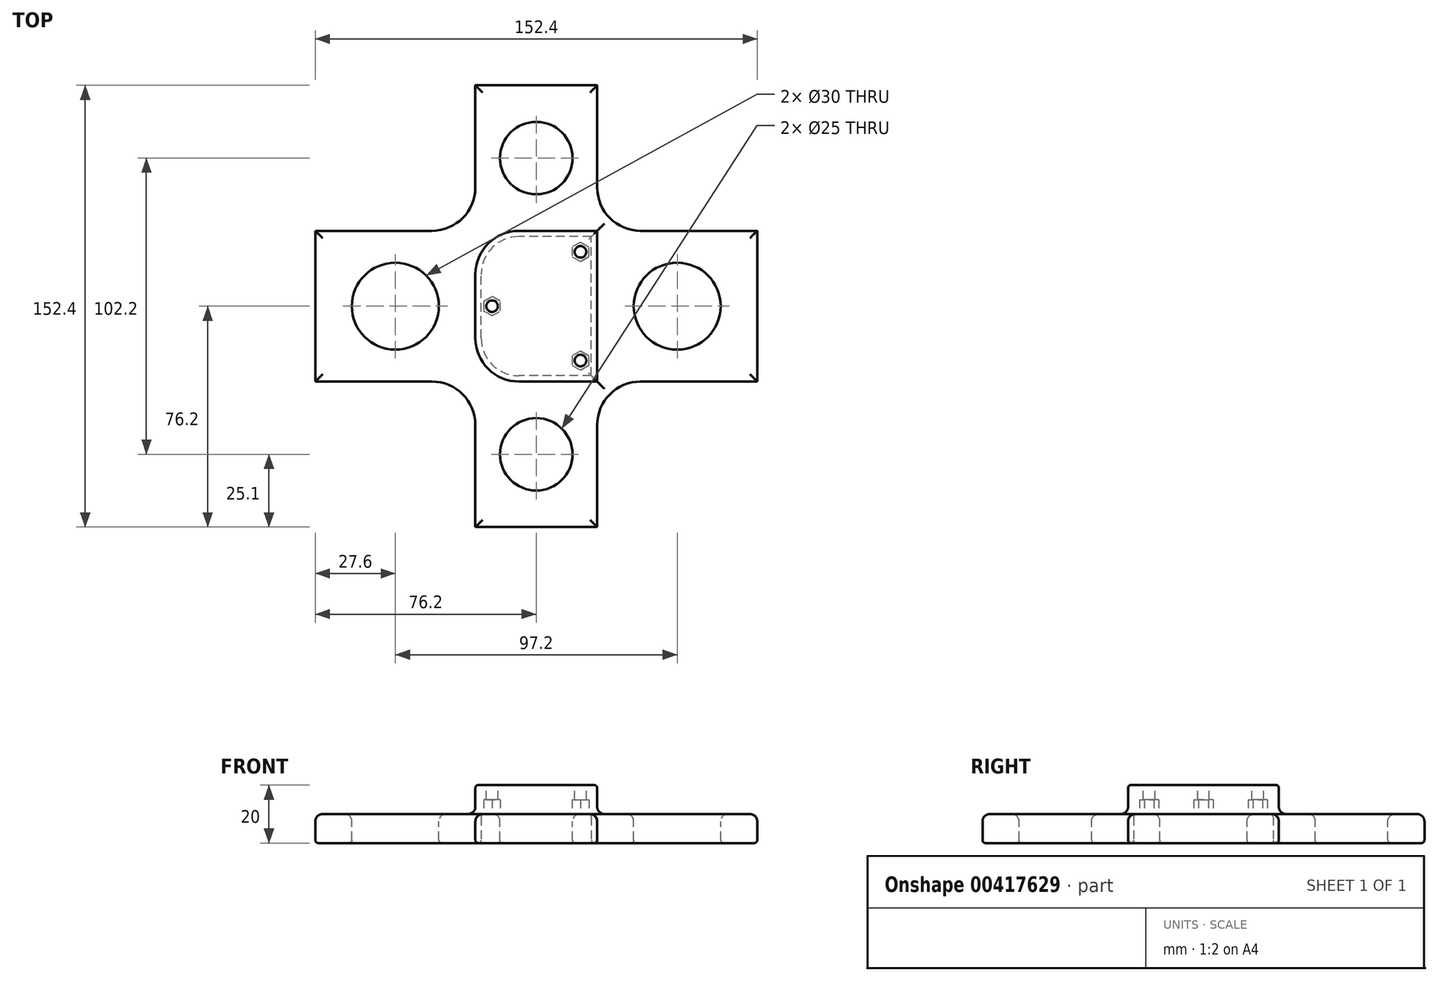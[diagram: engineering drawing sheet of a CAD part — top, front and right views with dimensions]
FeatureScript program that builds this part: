
annotation { "Feature Type Name" : "Feature", "Feature Type Description" : "" }
export const myFeature = defineFeature(function(context is Context, id is Id, definition is map)
    precondition{}
    {
        {
            var Q0;
            Q0=qCreatedBy(makeId("Top.planeOp"),FACE);
            var sketch = newSketch(context, id + "F0", { "sketchPlane" : qUnion([Q0])});
            skLineSegment(sketch, "E0.bottom", {"start": v(76.2, 76.2) * mm, "end": v(-76.2, 76.2) * mm});
            skLineSegment(sketch, "E0.top", {"start": v(76.2, -76.2) * mm, "end": v(-76.2, -76.2) * mm});
            skLineSegment(sketch, "E0.left", {"start": v(76.2, 76.2) * mm, "end": v(76.2, -76.2) * mm});
            skLineSegment(sketch, "E0.right", {"start": v(-76.2, 76.2) * mm, "end": v(-76.2, -76.2) * mm});
            skPoint(sketch, "E0.middle", {"position": v(0, 0) * mm});
            skSolve(sketch);
        }
        {
            var Q0;
            Q0 = qSketchRegion(id + "F0", true);
            extrude(context, id + "F1", {"entities" : qUnion([Q0]), "depth" : 10 * mm});
        }
        {
            var Q0;
            Q0=makeQuery(id+"F1.opExtrude","CAP_FACE",FACE,{"disambiguationData":[OSD([sQuery(id+"F0.wireOp",EDGE,"E0.bottom"),sQuery(id+"F0.wireOp",EDGE,"E0.top"),sQuery(id+"F0.wireOp",EDGE,"E0.left"),sQuery(id+"F0.wireOp",EDGE,"E0.right")])],"isStart":false});
            var sketch = newSketch(context, id + "F2", { "sketchPlane" : qUnion([Q0])});
            skLineSegment(sketch, "E1.bottom", {"start": v(21, -26) * mm, "end": v(-6, -26) * mm});
            skLineSegment(sketch, "E1.top", {"start": v(21, 26) * mm, "end": v(-6, 26) * mm});
            skLineSegment(sketch, "E1.left", {"start": v(21, -26) * mm, "end": v(21, 26) * mm});
            skLineSegment(sketch, "E1.right", {"start": v(-21, -11) * mm, "end": v(-21, 11) * mm});
            skPoint(sketch, "E1.middle", {"position": v(0, 0) * mm});
            skPoint(sketch, "E2.visualSharp", {"position": v(-21, 26) * mm});
            skArc(sketch, "E2.filletArc", {"start": v(-6, 26) * mm, "mid": v(-16.6, 21.6) * mm, "end": v(-21, 11) * mm});
            skPoint(sketch, "E3.visualSharp", {"position": v(-21, -26) * mm});
            skArc(sketch, "E3.filletArc", {"start": v(-21, -11) * mm, "mid": v(-16.6, -21.6) * mm, "end": v(-6, -26) * mm});
            skSolve(sketch);
        }
        {
            var Q0;
            Q0 = qSketchRegion(id + "F2", true);
            extrude(context, id + "F3", {"entities" : qUnion([Q0]), "operationType" : NewBodyOperationType.ADD, "depth" : 10 * mm});
        }
        {
            var Q0;
            Q0=makeQuery(id+"F1.opExtrude","CAP_FACE",FACE,{"disambiguationData":[OSD([sQuery(id+"F0.wireOp",EDGE,"E0.bottom"),sQuery(id+"F0.wireOp",EDGE,"E0.top"),sQuery(id+"F0.wireOp",EDGE,"E0.left"),sQuery(id+"F0.wireOp",EDGE,"E0.right")])],"isStart":false});
            var sketch = newSketch(context, id + "F4", { "sketchPlane" : qUnion([Q0])});
            skLineSegment(sketch, "E4.0", {"start": v(76.2, -76.2) * mm, "end": v(21, -76.2) * mm});
            skLineSegment(sketch, "E4.1", {"start": v(-76.2, 76.2) * mm, "end": v(-76.2, 26) * mm});
            skLineSegment(sketch, "E4.2", {"start": v(76.2, 76.2) * mm, "end": v(21, 76.2) * mm});
            skLineSegment(sketch, "E4.3", {"start": v(76.2, 76.2) * mm, "end": v(76.2, 26) * mm});
            skLineSegment(sketch, "E5", {"start": v(21, 26) * mm, "end": v(21, 76.2) * mm});
            skLineSegment(sketch, "E6", {"start": v(21, 26) * mm, "end": v(76.2, 26) * mm});
            skLineSegment(sketch, "E7", {"start": v(21, -26) * mm, "end": v(76.2, -26) * mm});
            skLineSegment(sketch, "E8", {"start": v(21, -26) * mm, "end": v(21, -76.2) * mm});
            skLineSegment(sketch, "E9", {"start": v(-21, -26) * mm, "end": v(-21, -76.2) * mm});
            skLineSegment(sketch, "E10", {"start": v(-21, -26) * mm, "end": v(-76.2, -26) * mm});
            skLineSegment(sketch, "E11", {"start": v(-21, 26) * mm, "end": v(-21, 76.2) * mm});
            skLineSegment(sketch, "E12", {"start": v(-21, 26) * mm, "end": v(-76.2, 26) * mm});
            skLineSegment(sketch, "E13.trimOffspring", {"start": v(-21, 76.2) * mm, "end": v(-76.2, 76.2) * mm});
            skLineSegment(sketch, "E14.trimOffspring", {"start": v(76.2, -26) * mm, "end": v(76.2, -76.2) * mm});
            skLineSegment(sketch, "E15.trimOffspring", {"start": v(-21, -76.2) * mm, "end": v(-76.2, -76.2) * mm});
            skLineSegment(sketch, "E16.trimOffspring", {"start": v(-76.2, -26) * mm, "end": v(-76.2, -76.2) * mm});
            skSolve(sketch);
        }
        {
            var Q0;
            Q0 = qSketchRegion(id + "F4", true);
            extrude(context, id + "F5", {"entities" : qUnion([Q0]), "operationType" : NewBodyOperationType.REMOVE, "endBound" : BoundingType.UP_TO_NEXT, "oppositeDirection" : true, "depth" : 25 * mm});
        }
        {
            var Q0;
            Q0=makeQuery(id+"F5.boolean.opBoolean","COPY",EDGE,{"derivedFrom":makeQuery(id+"F5.opExtrude","SWEPT_EDGE",EDGE,{"disambiguationData":[OSD([sQuery(id+"F0.wireOp",EDGE,"E0.bottom"),sQuery(id+"F4.wireOp",EDGE,"E11"),sQuery(id+"F4.wireOp",EDGE,"E13.trimOffspring")])]})});
            var Q1;
            Q1=makeQuery(id+"F5.boolean.opBoolean","COPY",EDGE,{"derivedFrom":makeQuery(id+"F5.opExtrude","SWEPT_EDGE",EDGE,{"disambiguationData":[OSD([sQuery(id+"F0.wireOp",EDGE,"E0.right"),sQuery(id+"F4.wireOp",EDGE,"E4.1"),sQuery(id+"F4.wireOp",EDGE,"E12")])]})});
            var Q2;
            Q2=makeQuery(id+"F5.boolean.opBoolean","COPY",EDGE,{"derivedFrom":makeQuery(id+"F5.opExtrude","SWEPT_EDGE",EDGE,{"disambiguationData":[OSD([sQuery(id+"F0.wireOp",EDGE,"E0.right"),sQuery(id+"F4.wireOp",EDGE,"E10"),sQuery(id+"F4.wireOp",EDGE,"E16.trimOffspring")])]})});
            var Q3;
            Q3=makeQuery(id+"F5.boolean.opBoolean","COPY",EDGE,{"derivedFrom":makeQuery(id+"F5.opExtrude","SWEPT_EDGE",EDGE,{"disambiguationData":[OSD([sQuery(id+"F0.wireOp",EDGE,"E0.top"),sQuery(id+"F4.wireOp",EDGE,"E9"),sQuery(id+"F4.wireOp",EDGE,"E15.trimOffspring")])]})});
            var Q4;
            Q4=makeQuery(id+"F5.boolean.opBoolean","COPY",EDGE,{"derivedFrom":makeQuery(id+"F5.opExtrude","SWEPT_EDGE",EDGE,{"disambiguationData":[OSD([sQuery(id+"F4.wireOp",EDGE,"E11"),sQuery(id+"F4.wireOp",EDGE,"E12")])]})});
            var Q5;
            Q5=makeQuery(id+"F5.boolean.opBoolean","COPY",EDGE,{"derivedFrom":makeQuery(id+"F5.opExtrude","SWEPT_EDGE",EDGE,{"disambiguationData":[OSD([sQuery(id+"F0.wireOp",EDGE,"E0.bottom"),sQuery(id+"F4.wireOp",EDGE,"E4.2"),sQuery(id+"F4.wireOp",EDGE,"E5")])]})});
            var Q6;
            Q6=makeQuery(id+"F5.boolean.opBoolean","COPY",EDGE,{"derivedFrom":makeQuery(id+"F5.opExtrude","SWEPT_EDGE",EDGE,{"disambiguationData":[OSD([sQuery(id+"F0.wireOp",EDGE,"E0.left"),sQuery(id+"F4.wireOp",EDGE,"E4.3"),sQuery(id+"F4.wireOp",EDGE,"E6")])]})});
            var Q7;
            Q7=makeQuery(id+"F5.boolean.opBoolean","COPY",EDGE,{"derivedFrom":makeQuery(id+"F5.opExtrude","SWEPT_EDGE",EDGE,{"disambiguationData":[OSD([sQuery(id+"F0.wireOp",EDGE,"E0.left"),sQuery(id+"F4.wireOp",EDGE,"E7"),sQuery(id+"F4.wireOp",EDGE,"E14.trimOffspring")])]})});
            var Q8;
            Q8=makeQuery(id+"F5.boolean.opBoolean","COPY",EDGE,{"derivedFrom":makeQuery(id+"F5.opExtrude","SWEPT_EDGE",EDGE,{"disambiguationData":[OSD([sQuery(id+"F0.wireOp",EDGE,"E0.top"),sQuery(id+"F4.wireOp",EDGE,"E4.0"),sQuery(id+"F4.wireOp",EDGE,"E8")])]})});
            var Q9;
            Q9=makeQuery(id+"F5.boolean.opBoolean","COPY",EDGE,{"derivedFrom":makeQuery(id+"F5.opExtrude","SWEPT_EDGE",EDGE,{"disambiguationData":[OSD([sQuery(id+"F2.wireOp",EDGE,"E1.top"),sQuery(id+"F2.wireOp",EDGE,"E1.left"),sQuery(id+"F4.wireOp",EDGE,"E5"),sQuery(id+"F4.wireOp",EDGE,"E6")])]})});
            var Q10;
            Q10=makeQuery(id+"F5.boolean.opBoolean","COPY",EDGE,{"derivedFrom":makeQuery(id+"F5.opExtrude","SWEPT_EDGE",EDGE,{"disambiguationData":[OSD([sQuery(id+"F2.wireOp",EDGE,"E1.bottom"),sQuery(id+"F2.wireOp",EDGE,"E1.left"),sQuery(id+"F4.wireOp",EDGE,"E7"),sQuery(id+"F4.wireOp",EDGE,"E8")])]})});
            var Q11;
            Q11=makeQuery(id+"F5.boolean.opBoolean","COPY",EDGE,{"derivedFrom":makeQuery(id+"F5.opExtrude","SWEPT_EDGE",EDGE,{"disambiguationData":[OSD([sQuery(id+"F4.wireOp",EDGE,"E9"),sQuery(id+"F4.wireOp",EDGE,"E10")])]})});
            fillet(context, id + "F6", {"entities" : qUnion([Q0, Q1, Q2, Q3, Q4, Q5, Q6, Q7, Q8, Q9, Q10, Q11]), "radius" : 15 * mm, "tangentPropagation" : true, "allowEdgeOverflow" : false});
        }
        {
            var Q0;
            {var subQ1=sQuery(id+"F0.wireOp",EDGE,"E0.left");var subQ3=sQuery(id+"F0.wireOp",EDGE,"E0.right");var subQ4=sQuery(id+"F0.wireOp",EDGE,"E0.top");var subQ5=sQuery(id+"F0.wireOp",EDGE,"E0.bottom");var subQ6=makeQuery(id+"F1.opExtrude","CAP_FACE",FACE,{"disambiguationData":[OSD([subQ5,subQ4,subQ1,subQ3])],"isStart":false});var subQ12=subQ6;Q0=makeQuery(id+"F6.opFillet","MERGE",FACE,{"derivedFrom":[makeQuery(id+"F5.boolean.opBoolean","SPLIT",FACE,{"disambiguationData":[TD([makeQuery(id+"F1.opExtrude","SWEPT_FACE",FACE,{"disambiguationData":[OSD([subQ5])]})])],"derivedFrom":subQ12}),makeQuery(id+"F5.boolean.opBoolean","SPLIT",FACE,{"disambiguationData":[TD([makeQuery(id+"F1.opExtrude","SWEPT_FACE",FACE,{"disambiguationData":[OSD([subQ1])]})])],"derivedFrom":subQ12})]});}
            var sketch = newSketch(context, id + "F7", { "sketchPlane" : qUnion([Q0])});
            skLineSegment(sketch, "E17", {"start": v(0, 26) * mm, "end": v(0, 76.2) * mm, "construction": true});
            skLineSegment(sketch, "E18", {"start": v(-76.2, 0) * mm, "end": v(-21, 0) * mm, "construction": true});
            skLineSegment(sketch, "E19", {"start": v(0, -76.2) * mm, "end": v(0, -26) * mm, "construction": true});
            skLineSegment(sketch, "E20", {"start": v(76.2, 0) * mm, "end": v(21, 0) * mm, "construction": true});
            skCircle(sketch, "E21", {"center": v(-48.6, 0) * mm, "radius": 15 * mm});
            skCircle(sketch, "E22", {"center": v(0, 51.1) * mm, "radius": 12.5 * mm});
            skCircle(sketch, "E23", {"center": v(0, -51.1) * mm, "radius": 12.5 * mm});
            skCircle(sketch, "E24", {"center": v(48.6, 0) * mm, "radius": 15 * mm});
            skSolve(sketch);
        }
        {
            var Q0;
            Q0 = qSketchRegion(id + "F7", true);
            extrude(context, id + "F8", {"entities" : qUnion([Q0]), "operationType" : NewBodyOperationType.REMOVE, "endBound" : BoundingType.UP_TO_NEXT, "oppositeDirection" : true, "depth" : 25 * mm});
        }
        {
            var Q0;
            Q0=makeQuery(id+"F1.opExtrude","CAP_FACE",FACE,{"disambiguationData":[OSD([sQuery(id+"F0.wireOp",EDGE,"E0.bottom"),sQuery(id+"F0.wireOp",EDGE,"E0.top"),sQuery(id+"F0.wireOp",EDGE,"E0.left"),sQuery(id+"F0.wireOp",EDGE,"E0.right")])],"isStart":true});
            var sketch = newSketch(context, id + "F9", { "sketchPlane" : qUnion([Q0])});
            skLineSegment(sketch, "E25.0", {"start": v(21, 26) * mm, "end": v(-6, 26) * mm, "construction": true});
            skLineSegment(sketch, "E25.1", {"start": v(21, -26) * mm, "end": v(-6, -26) * mm, "construction": true});
            skLineSegment(sketch, "E25.2", {"start": v(21, 26) * mm, "end": v(21, -26) * mm, "construction": true});
            skLineSegment(sketch, "E25.3", {"start": v(-21, 11) * mm, "end": v(-21, -11) * mm, "construction": true});
            skPoint(sketch, "E25.4", {"position": v(0, 0) * mm});
            skPoint(sketch, "E25.5", {"position": v(-21, -26) * mm});
            skArc(sketch, "E25.6", {"start": v(-6, -26) * mm, "mid": v(-16.6, -21.6) * mm, "end": v(-21, -11) * mm, "construction": true});
            skPoint(sketch, "E25.7", {"position": v(-21, 26) * mm});
            skArc(sketch, "E25.8", {"start": v(-21, 11) * mm, "mid": v(-16.6, 21.6) * mm, "end": v(-6, 26) * mm, "construction": true});
            skLineSegment(sketch, "E26.0", {"start": v(-19, 11) * mm, "end": v(-19, -11) * mm});
            skLineSegment(sketch, "E26.1", {"start": v(19, 24) * mm, "end": v(-6, 24) * mm});
            skLineSegment(sketch, "E26.2", {"start": v(19, 24) * mm, "end": v(19, -24) * mm});
            skArc(sketch, "E26.3", {"start": v(-19, 11) * mm, "mid": v(-15.2, 20.2) * mm, "end": v(-6, 24) * mm});
            skLineSegment(sketch, "E26.4", {"start": v(19, -24) * mm, "end": v(-6, -24) * mm});
            skArc(sketch, "E26.5", {"start": v(-6, -24) * mm, "mid": v(-15.2, -20.2) * mm, "end": v(-19, -11) * mm});
            skSolve(sketch);
        }
        {
            var Q0;
            Q0 = qSketchRegion(id + "F9", true);
            extrude(context, id + "F10", {"entities" : qUnion([Q0]), "operationType" : NewBodyOperationType.REMOVE, "oppositeDirection" : true, "depth" : 10 * mm});
        }
        {
            var Q0;
            {var subQ1=sQuery(id+"F0.wireOp",EDGE,"E0.left");var subQ3=sQuery(id+"F0.wireOp",EDGE,"E0.right");var subQ4=sQuery(id+"F0.wireOp",EDGE,"E0.top");var subQ5=sQuery(id+"F0.wireOp",EDGE,"E0.bottom");var subQ6=makeQuery(id+"F1.opExtrude","CAP_FACE",FACE,{"disambiguationData":[OSD([subQ5,subQ4,subQ1,subQ3])],"isStart":false});var subQ12=subQ6;Q0=makeQuery(id+"F6.opFillet","MERGE",FACE,{"derivedFrom":[makeQuery(id+"F5.boolean.opBoolean","SPLIT",FACE,{"disambiguationData":[TD([makeQuery(id+"F1.opExtrude","SWEPT_FACE",FACE,{"disambiguationData":[OSD([subQ5])]})])],"derivedFrom":subQ12}),makeQuery(id+"F5.boolean.opBoolean","SPLIT",FACE,{"disambiguationData":[TD([makeQuery(id+"F1.opExtrude","SWEPT_FACE",FACE,{"disambiguationData":[OSD([subQ1])]})])],"derivedFrom":subQ12})]});}
            fillet(context, id + "F11", {"entities" : qUnion([Q0]), "radius" : 2.5 * mm, "tangentPropagation" : true, "allowEdgeOverflow" : false});
        }
        {
            var Q0;
            Q0=makeQuery(id+"F3.opExtrude","CAP_FACE",FACE,{"disambiguationData":[OSD([sQuery(id+"F2.wireOp",EDGE,"E1.bottom"),sQuery(id+"F2.wireOp",EDGE,"E1.top"),sQuery(id+"F2.wireOp",EDGE,"E1.left"),sQuery(id+"F2.wireOp",EDGE,"E1.right"),sQuery(id+"F2.wireOp",EDGE,"E2.filletArc"),sQuery(id+"F2.wireOp",EDGE,"E3.filletArc")])],"isStart":false});
            var Q1;
            Q1=makeQuery(id+"F1.opExtrude","CAP_FACE",FACE,{"disambiguationData":[OSD([sQuery(id+"F0.wireOp",EDGE,"E0.bottom"),sQuery(id+"F0.wireOp",EDGE,"E0.top"),sQuery(id+"F0.wireOp",EDGE,"E0.left"),sQuery(id+"F0.wireOp",EDGE,"E0.right")])],"isStart":true});
            var Q2;
            Q2=makeQuery(id+"F10.boolean.opBoolean","COPY",FACE,{"derivedFrom":makeQuery(id+"F10.opExtrude","CAP_FACE",FACE,{"disambiguationData":[OSD([sQuery(id+"F9.wireOp",EDGE,"E26.0"),sQuery(id+"F9.wireOp",EDGE,"E26.1"),sQuery(id+"F9.wireOp",EDGE,"E26.2"),sQuery(id+"F9.wireOp",EDGE,"E26.3"),sQuery(id+"F9.wireOp",EDGE,"E26.4"),sQuery(id+"F9.wireOp",EDGE,"E26.5")])],"isStart":false})});
            fillet(context, id + "F12", {"entities" : qUnion([Q0, Q1, Q2]), "radius" : 1 * mm, "tangentPropagation" : true, "allowEdgeOverflow" : false});
        }
        {
            var Q0;
            Q0=makeQuery(id+"F3.opExtrude","CAP_FACE",FACE,{"disambiguationData":[OSD([sQuery(id+"F2.wireOp",EDGE,"E1.bottom"),sQuery(id+"F2.wireOp",EDGE,"E1.top"),sQuery(id+"F2.wireOp",EDGE,"E1.left"),sQuery(id+"F2.wireOp",EDGE,"E1.right"),sQuery(id+"F2.wireOp",EDGE,"E2.filletArc"),sQuery(id+"F2.wireOp",EDGE,"E3.filletArc")])],"isStart":false});
            var sketch = newSketch(context, id + "F13", { "sketchPlane" : qUnion([Q0])});
            skLineSegment(sketch, "E27", {"start": v(15.25, 18.75) * mm, "end": v(15.25, -18.75) * mm, "construction": true});
            skLineSegment(sketch, "E28", {"start": v(15.25, 0) * mm, "end": v(0, 0) * mm, "construction": true});
            skLineSegment(sketch, "E29", {"start": v(0, 0) * mm, "end": v(-15.25, 0) * mm, "construction": true});
            skCircle(sketch, "E30", {"center": v(-15.25, 0) * mm, "radius": 2 * mm});
            skCircle(sketch, "E31", {"center": v(15.25, 18.75) * mm, "radius": 2 * mm});
            skCircle(sketch, "E32", {"center": v(15.25, -18.75) * mm, "radius": 2 * mm});
            skSolve(sketch);
        }
        {
            var Q0;
            Q0 = qSketchRegion(id + "F13", true);
            extrude(context, id + "F14", {"entities" : qUnion([Q0]), "operationType" : NewBodyOperationType.REMOVE, "endBound" : BoundingType.UP_TO_NEXT, "oppositeDirection" : true, "depth" : 25 * mm});
        }
        {
            var Q0;
            Q0=makeQuery(id+"F10.boolean.opBoolean","COPY",FACE,{"derivedFrom":makeQuery(id+"F10.opExtrude","CAP_FACE",FACE,{"disambiguationData":[OSD([sQuery(id+"F9.wireOp",EDGE,"E26.0"),sQuery(id+"F9.wireOp",EDGE,"E26.1"),sQuery(id+"F9.wireOp",EDGE,"E26.2"),sQuery(id+"F9.wireOp",EDGE,"E26.3"),sQuery(id+"F9.wireOp",EDGE,"E26.4"),sQuery(id+"F9.wireOp",EDGE,"E26.5")])],"isStart":false})});
            var sketch = newSketch(context, id + "F15", { "sketchPlane" : qUnion([Q0])});
            skCircle(sketch, "E33.cCircle", {"center": v(-15.25, 0) * mm, "radius": 2.88 * mm, "construction": true});
            skLineSegment(sketch, "E33.0", {"start": v(-12.38, 1.66) * mm, "end": v(-12.38, -1.66) * mm});
            skLineSegment(sketch, "E33.1", {"start": v(-12.37, -1.66) * mm, "end": v(-15.25, -3.32) * mm});
            skLineSegment(sketch, "E33.2", {"start": v(-15.25, -3.32) * mm, "end": v(-18.13, -1.66) * mm});
            skLineSegment(sketch, "E33.3", {"start": v(-18.13, -1.66) * mm, "end": v(-18.13, 1.66) * mm});
            skLineSegment(sketch, "E33.4", {"start": v(-18.13, 1.66) * mm, "end": v(-15.25, 3.32) * mm});
            skLineSegment(sketch, "E33.5", {"start": v(-15.25, 3.32) * mm, "end": v(-12.37, 1.66) * mm});
            skPoint(sketch, "E33.0.midPoint", {"position": v(-12.38, 0) * mm});
            skCircle(sketch, "E34.cCircle", {"center": v(15.25, 18.75) * mm, "radius": 2.88 * mm, "construction": true});
            skLineSegment(sketch, "E34.0", {"start": v(12.38, 17.1) * mm, "end": v(12.38, 20.4) * mm});
            skLineSegment(sketch, "E34.1", {"start": v(12.38, 20.4) * mm, "end": v(15.25, 22.07) * mm});
            skLineSegment(sketch, "E34.2", {"start": v(15.25, 22.07) * mm, "end": v(18.13, 20.4) * mm});
            skLineSegment(sketch, "E34.3", {"start": v(18.13, 20.4) * mm, "end": v(18.13, 17.1) * mm});
            skLineSegment(sketch, "E34.4", {"start": v(18.13, 17.1) * mm, "end": v(15.25, 15.43) * mm});
            skLineSegment(sketch, "E34.5", {"start": v(15.25, 15.43) * mm, "end": v(12.38, 17.1) * mm});
            skPoint(sketch, "E34.0.midPoint", {"position": v(12.38, 18.75) * mm});
            skCircle(sketch, "E35.cCircle", {"center": v(15.25, -18.75) * mm, "radius": 2.88 * mm, "construction": true});
            skLineSegment(sketch, "E35.0", {"start": v(12.37, -20.4) * mm, "end": v(12.37, -17.1) * mm});
            skLineSegment(sketch, "E35.1", {"start": v(12.37, -17.1) * mm, "end": v(15.25, -15.43) * mm});
            skLineSegment(sketch, "E35.2", {"start": v(15.25, -15.43) * mm, "end": v(18.12, -17.1) * mm});
            skLineSegment(sketch, "E35.3", {"start": v(18.12, -17.1) * mm, "end": v(18.12, -20.4) * mm});
            skLineSegment(sketch, "E35.4", {"start": v(18.12, -20.4) * mm, "end": v(15.25, -22.07) * mm});
            skLineSegment(sketch, "E35.5", {"start": v(15.25, -22.07) * mm, "end": v(12.37, -20.4) * mm});
            skPoint(sketch, "E35.0.midPoint", {"position": v(12.37, -18.75) * mm});
            skSolve(sketch);
        }
        {
            var Q0;
            Q0 = qSketchRegion(id + "F15", true);
            extrude(context, id + "F16", {"entities" : qUnion([Q0]), "operationType" : NewBodyOperationType.REMOVE, "oppositeDirection" : true, "depth" : 5 * mm});
        }
    });
